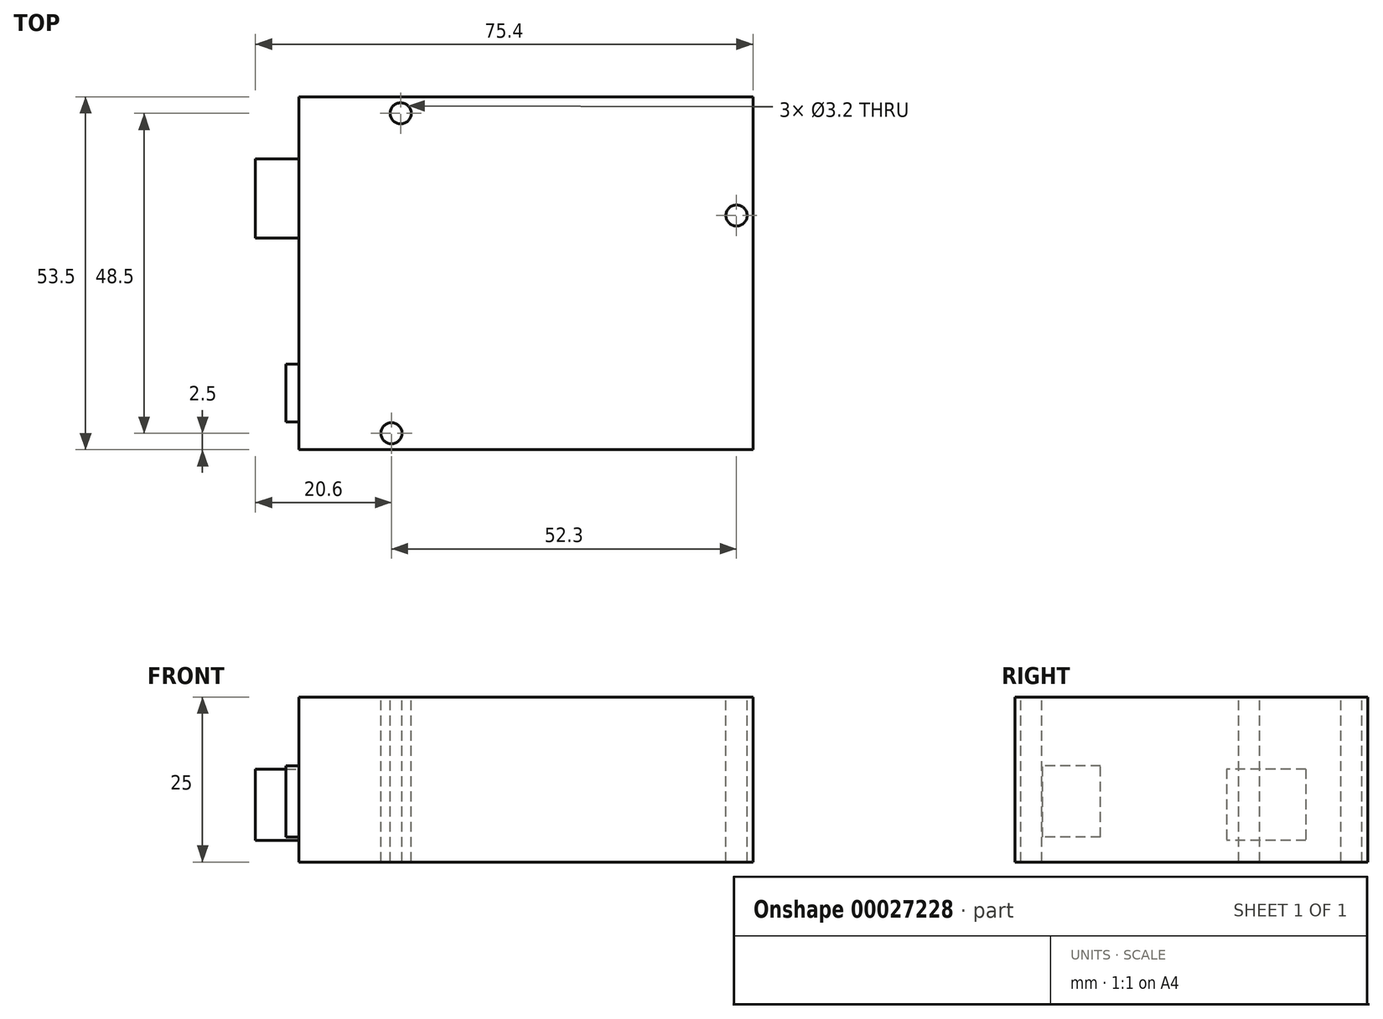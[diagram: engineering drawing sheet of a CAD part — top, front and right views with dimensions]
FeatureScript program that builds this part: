
annotation { "Feature Type Name" : "Feature", "Feature Type Description" : "" }
export const myFeature = defineFeature(function(context is Context, id is Id, definition is map)
    precondition{}
    {
        {
            var Q0;
            Q0=qCreatedBy(makeId("Top.planeOp"),FACE);
            var sketch = newSketch(context, id + "F0", { "sketchPlane" : qUnion([Q0])});
            skLineSegment(sketch, "E0.rect.bottom", {"start": v(34.4, 26.75) * mm, "end": v(-34.4, 26.75) * mm});
            skLineSegment(sketch, "E0.rect.top", {"start": v(34.4, -26.75) * mm, "end": v(-34.4, -26.75) * mm});
            skLineSegment(sketch, "E0.rect.left", {"start": v(34.4, 26.75) * mm, "end": v(34.4, -26.75) * mm});
            skLineSegment(sketch, "E0.rect.right", {"start": v(-34.4, 26.75) * mm, "end": v(-34.4, -26.75) * mm});
            skPoint(sketch, "E0.rect.middle", {"position": v(0, 0) * mm});
            skSolve(sketch);
        }
        {
            var Q0;
            Q0 = qSketchRegion(id + "F0", true);
            extrude(context, id + "F1", {"entities" : qUnion([Q0]), "depth" : 25 * mm});
        }
        {
            var Q0;
            Q0=makeQuery(id+"F1.opExtrude","CAP_FACE",FACE,{"disambiguationData":[OSD([sQuery(id+"F0.wireOp",EDGE,"E0.rect.bottom"),sQuery(id+"F0.wireOp",EDGE,"E0.rect.top"),sQuery(id+"F0.wireOp",EDGE,"E0.rect.left"),sQuery(id+"F0.wireOp",EDGE,"E0.rect.right")])],"isStart":false});
            var sketch = newSketch(context, id + "F2", { "sketchPlane" : qUnion([Q0])});
            skCircle(sketch, "E1", {"center": v(-19, 24.25) * mm, "radius": 1.6 * mm});
            skCircle(sketch, "E2", {"center": v(31.9, 8.75) * mm, "radius": 1.6 * mm});
            skCircle(sketch, "E3", {"center": v(-20.4, -24.25) * mm, "radius": 1.6 * mm});
            skSolve(sketch);
        }
        {
            var Q0;
            Q0 = qSketchRegion(id + "F2", true);
            extrude(context, id + "F3", {"entities" : qUnion([Q0]), "operationType" : NewBodyOperationType.REMOVE, "oppositeDirection" : true, "depth" : 25 * mm});
        }
        {
            var Q0;
            Q0=makeQuery(id+"F1.opExtrude","SWEPT_FACE",FACE,{"disambiguationData":[OSD([sQuery(id+"F0.wireOp",EDGE,"E0.rect.right")])]});
            var sketch = newSketch(context, id + "F4", { "sketchPlane" : qUnion([Q0])});
            skLineSegment(sketch, "E4.bottom", {"start": v(-17.35, 14.1) * mm, "end": v(-5.35, 14.1) * mm});
            skLineSegment(sketch, "E4.top", {"start": v(-17.35, 3.3) * mm, "end": v(-5.35, 3.3) * mm});
            skLineSegment(sketch, "E4.left", {"start": v(-17.35, 14.1) * mm, "end": v(-17.35, 3.3) * mm});
            skLineSegment(sketch, "E4.right", {"start": v(-5.35, 14.1) * mm, "end": v(-5.35, 3.3) * mm});
            skSolve(sketch);
        }
        {
            var Q0;
            Q0 = qSketchRegion(id + "F4", true);
            extrude(context, id + "F5", {"entities" : qUnion([Q0]), "operationType" : NewBodyOperationType.ADD, "depth" : 6.6 * mm});
        }
        {
            var Q0;
            Q0=makeQuery(id+"F1.opExtrude","SWEPT_FACE",FACE,{"disambiguationData":[OSD([sQuery(id+"F0.wireOp",EDGE,"E0.rect.right")])]});
            var sketch = newSketch(context, id + "F6", { "sketchPlane" : qUnion([Q0])});
            skLineSegment(sketch, "E5.bottom", {"start": v(13.75, 3.78) * mm, "end": v(22.55, 3.78) * mm});
            skLineSegment(sketch, "E5.top", {"start": v(13.75, 14.58) * mm, "end": v(22.55, 14.58) * mm});
            skLineSegment(sketch, "E5.left", {"start": v(13.75, 3.78) * mm, "end": v(13.75, 14.58) * mm});
            skLineSegment(sketch, "E5.right", {"start": v(22.55, 3.78) * mm, "end": v(22.55, 14.58) * mm});
            skSolve(sketch);
        }
        {
            var Q0;
            Q0 = qSketchRegion(id + "F6", true);
            extrude(context, id + "F7", {"entities" : qUnion([Q0]), "operationType" : NewBodyOperationType.ADD, "depth" : 2 * mm});
        }
    });
